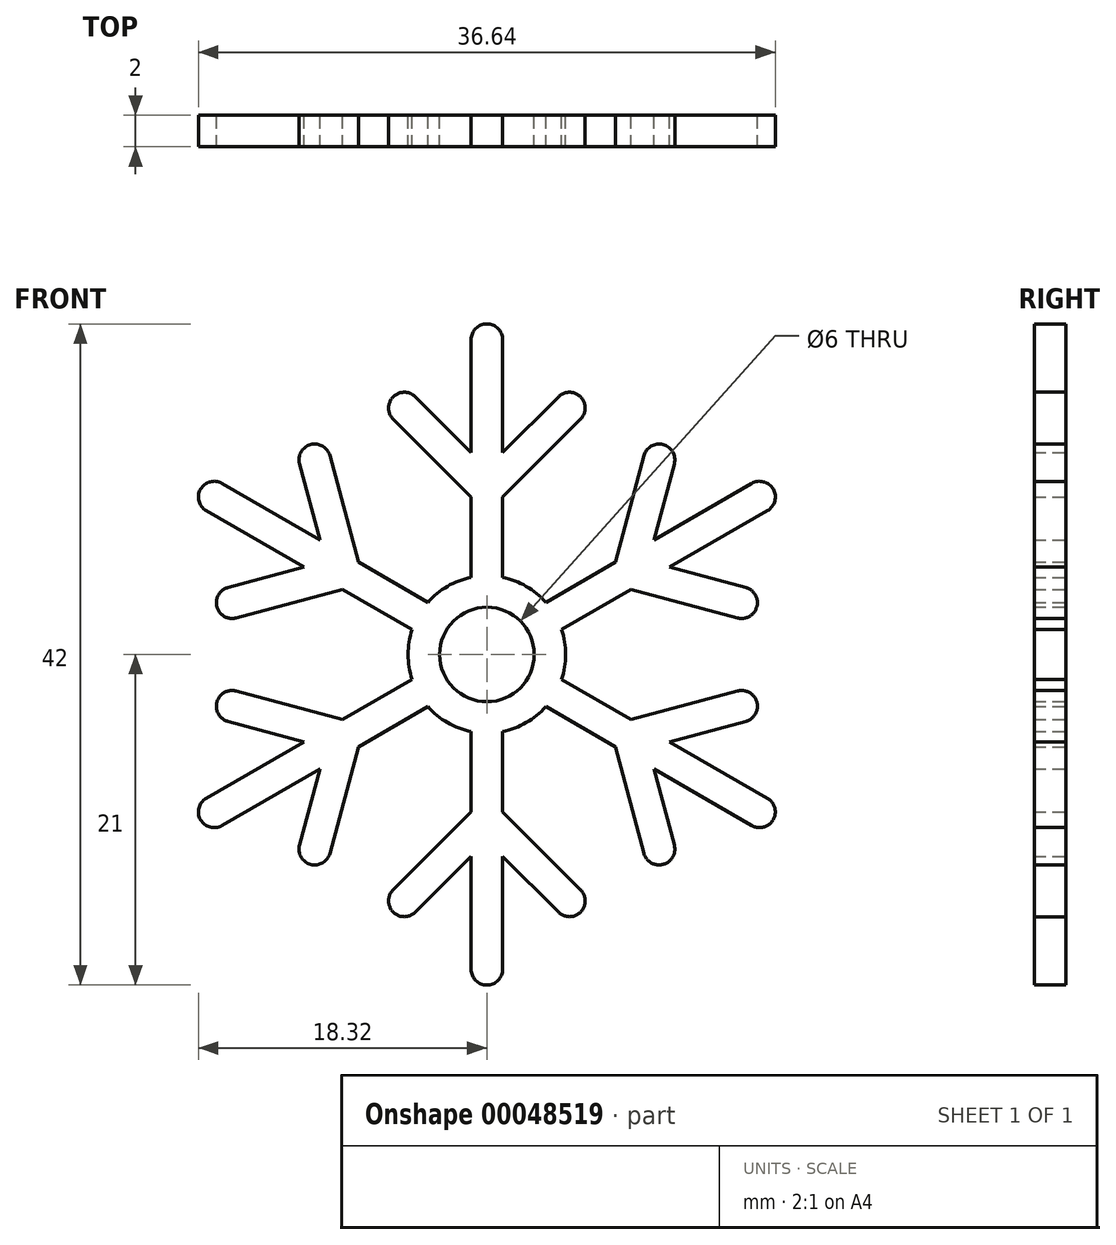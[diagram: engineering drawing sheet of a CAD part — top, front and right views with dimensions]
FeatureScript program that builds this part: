
annotation { "Feature Type Name" : "Feature", "Feature Type Description" : "" }
export const myFeature = defineFeature(function(context is Context, id is Id, definition is map)
    precondition{}
    {
        {
            var Q0;
            Q0=qCreatedBy(makeId("Front.planeOp"),FACE);
            var sketch = newSketch(context, id + "F0", { "sketchPlane" : qUnion([Q0])});
            skLineSegment(sketch, "E0", {"start": v(0, 14.92) * mm, "end": v(0, -7.22) * mm, "construction": true});
            skArc(sketch, "E1", {"start": v(-1, 4.9) * mm, "mid": v(-2.5, 4.33) * mm, "end": v(-3.74, 3.32) * mm});
            skCircle(sketch, "E2", {"center": v(0, 0) * mm, "radius": 3 * mm});
            skLineSegment(sketch, "E3", {"start": v(-1, 4.9) * mm, "end": v(-1, 10) * mm});
            skLineSegment(sketch, "E4", {"start": v(-1, 10) * mm, "end": v(-5.95, 14.95) * mm});
            skArc(sketch, "E5", {"start": v(-5.95, 14.95) * mm, "mid": v(-5.95, 16.36) * mm, "end": v(-4.54, 16.36) * mm});
            skLineSegment(sketch, "E6", {"start": v(-4.54, 16.36) * mm, "end": v(-1, 12.83) * mm});
            skLineSegment(sketch, "E7", {"start": v(-1, 12.83) * mm, "end": v(-1, 20) * mm});
            skArc(sketch, "E8", {"start": v(-1, 20) * mm, "mid": v(0.06, 21) * mm, "end": v(1, 19.87) * mm});
            skLineSegment(sketch, "E9.MirrorCS", {"start": v(1, 12.83) * mm, "end": v(1, 20) * mm});
            skLineSegment(sketch, "E10.MirrorCS", {"start": v(4.54, 16.36) * mm, "end": v(1, 12.83) * mm});
            skArc(sketch, "E11.MirrorCS", {"start": v(5.95, 14.95) * mm, "mid": v(5.95, 16.36) * mm, "end": v(4.54, 16.36) * mm});
            skLineSegment(sketch, "E12.MirrorCS", {"start": v(1, 10) * mm, "end": v(5.95, 14.95) * mm});
            skLineSegment(sketch, "E13.MirrorCS", {"start": v(1, 4.9) * mm, "end": v(1, 10) * mm});
            skPoint(sketch, "E14.orphan", {"position": v(1, 2.83) * mm});
            skPoint(sketch, "E15.orphan", {"position": v(-1, 2.83) * mm});
            skLineSegment(sketch, "E16.1.0", {"start": v(-3.74, 3.32) * mm, "end": v(-8.16, 5.87) * mm});
            skLineSegment(sketch, "E16.1.1", {"start": v(-8.16, 5.87) * mm, "end": v(-9.97, 12.63) * mm});
            skArc(sketch, "E16.1.2", {"start": v(-9.97, 12.63) * mm, "mid": v(-11.2, 13.33) * mm, "end": v(-11.9, 12.1) * mm});
            skLineSegment(sketch, "E16.1.3", {"start": v(-11.9, 12.1) * mm, "end": v(-10.6, 7.28) * mm});
            skLineSegment(sketch, "E16.1.4", {"start": v(-10.6, 7.28) * mm, "end": v(-16.82, 10.87) * mm});
            skArc(sketch, "E16.1.5", {"start": v(-17.82, 9.13) * mm, "mid": v(-18.15, 10.56) * mm, "end": v(-16.71, 10.8) * mm});
            skLineSegment(sketch, "E16.1.6", {"start": v(-11.6, 5.55) * mm, "end": v(-17.82, 9.13) * mm});
            skLineSegment(sketch, "E16.1.7", {"start": v(-16.44, 4.25) * mm, "end": v(-11.6, 5.55) * mm});
            skArc(sketch, "E16.1.8", {"start": v(-15.92, 2.32) * mm, "mid": v(-17.15, 3.03) * mm, "end": v(-16.44, 4.25) * mm});
            skLineSegment(sketch, "E16.1.9", {"start": v(-9.16, 4.13) * mm, "end": v(-15.92, 2.32) * mm});
            skLineSegment(sketch, "E16.1.10", {"start": v(-4.74, 1.58) * mm, "end": v(-9.16, 4.13) * mm});
            skLineSegment(sketch, "E16.2.0", {"start": v(-4.74, -1.58) * mm, "end": v(-9.16, -4.13) * mm});
            skLineSegment(sketch, "E16.2.1", {"start": v(-9.16, -4.13) * mm, "end": v(-15.92, -2.32) * mm});
            skArc(sketch, "E16.2.2", {"start": v(-15.92, -2.32) * mm, "mid": v(-17.15, -3.03) * mm, "end": v(-16.44, -4.25) * mm});
            skLineSegment(sketch, "E16.2.3", {"start": v(-16.44, -4.25) * mm, "end": v(-11.6, -5.55) * mm});
            skLineSegment(sketch, "E16.2.4", {"start": v(-11.6, -5.55) * mm, "end": v(-17.82, -9.13) * mm});
            skArc(sketch, "E16.2.5", {"start": v(-16.82, -10.87) * mm, "mid": v(-18.22, -10.44) * mm, "end": v(-17.7, -9.08) * mm});
            skLineSegment(sketch, "E16.2.6", {"start": v(-10.6, -7.28) * mm, "end": v(-16.82, -10.87) * mm});
            skLineSegment(sketch, "E16.2.7", {"start": v(-11.9, -12.1) * mm, "end": v(-10.6, -7.28) * mm});
            skArc(sketch, "E16.2.8", {"start": v(-9.97, -12.63) * mm, "mid": v(-11.2, -13.33) * mm, "end": v(-11.9, -12.1) * mm});
            skLineSegment(sketch, "E16.2.9", {"start": v(-8.16, -5.87) * mm, "end": v(-9.97, -12.63) * mm});
            skLineSegment(sketch, "E16.2.10", {"start": v(-3.74, -3.32) * mm, "end": v(-8.16, -5.87) * mm});
            skLineSegment(sketch, "E17.1.3.0", {"start": v(-1, -4.9) * mm, "end": v(-1, -10) * mm});
            skLineSegment(sketch, "E17.3.3.0", {"start": v(-1, -10) * mm, "end": v(-5.95, -14.95) * mm});
            skArc(sketch, "E17.6.3.0", {"start": v(-5.95, -14.95) * mm, "mid": v(-5.95, -16.36) * mm, "end": v(-4.54, -16.36) * mm});
            skLineSegment(sketch, "E17.10.3.0", {"start": v(-4.54, -16.36) * mm, "end": v(-1, -12.83) * mm});
            skLineSegment(sketch, "E17.13.3.0", {"start": v(-1, -12.83) * mm, "end": v(-1, -20) * mm});
            skArc(sketch, "E17.16.3.0", {"start": v(1, -20) * mm, "mid": v(-0.06, -21) * mm, "end": v(-1, -19.87) * mm});
            skLineSegment(sketch, "E17.20.3.0", {"start": v(1, -12.83) * mm, "end": v(1, -20) * mm});
            skLineSegment(sketch, "E17.23.3.0", {"start": v(4.54, -16.36) * mm, "end": v(1, -12.83) * mm});
            skArc(sketch, "E17.26.3.0", {"start": v(5.95, -14.95) * mm, "mid": v(5.95, -16.36) * mm, "end": v(4.54, -16.36) * mm});
            skLineSegment(sketch, "E17.30.3.0", {"start": v(1, -10) * mm, "end": v(5.95, -14.95) * mm});
            skLineSegment(sketch, "E17.33.3.0", {"start": v(1, -4.9) * mm, "end": v(1, -10) * mm});
            skLineSegment(sketch, "E17.1.4.0", {"start": v(3.74, -3.32) * mm, "end": v(8.16, -5.87) * mm});
            skLineSegment(sketch, "E17.3.4.0", {"start": v(8.16, -5.87) * mm, "end": v(9.97, -12.63) * mm});
            skArc(sketch, "E17.6.4.0", {"start": v(9.97, -12.63) * mm, "mid": v(11.2, -13.33) * mm, "end": v(11.9, -12.1) * mm});
            skLineSegment(sketch, "E17.10.4.0", {"start": v(11.9, -12.1) * mm, "end": v(10.6, -7.28) * mm});
            skLineSegment(sketch, "E17.13.4.0", {"start": v(10.6, -7.28) * mm, "end": v(16.82, -10.87) * mm});
            skArc(sketch, "E17.16.4.0", {"start": v(17.82, -9.13) * mm, "mid": v(18.15, -10.56) * mm, "end": v(16.71, -10.8) * mm});
            skLineSegment(sketch, "E17.20.4.0", {"start": v(11.6, -5.55) * mm, "end": v(17.82, -9.13) * mm});
            skLineSegment(sketch, "E17.23.4.0", {"start": v(16.44, -4.25) * mm, "end": v(11.6, -5.55) * mm});
            skArc(sketch, "E17.26.4.0", {"start": v(15.92, -2.32) * mm, "mid": v(17.15, -3.03) * mm, "end": v(16.44, -4.25) * mm});
            skLineSegment(sketch, "E17.30.4.0", {"start": v(9.16, -4.13) * mm, "end": v(15.92, -2.32) * mm});
            skLineSegment(sketch, "E17.33.4.0", {"start": v(4.74, -1.58) * mm, "end": v(9.16, -4.13) * mm});
            skLineSegment(sketch, "E17.1.5.0", {"start": v(4.74, 1.58) * mm, "end": v(9.16, 4.13) * mm});
            skLineSegment(sketch, "E17.3.5.0", {"start": v(9.16, 4.13) * mm, "end": v(15.92, 2.32) * mm});
            skArc(sketch, "E17.6.5.0", {"start": v(15.92, 2.32) * mm, "mid": v(17.15, 3.03) * mm, "end": v(16.44, 4.25) * mm});
            skLineSegment(sketch, "E17.10.5.0", {"start": v(16.44, 4.25) * mm, "end": v(11.6, 5.55) * mm});
            skLineSegment(sketch, "E17.13.5.0", {"start": v(11.6, 5.55) * mm, "end": v(17.82, 9.13) * mm});
            skArc(sketch, "E17.16.5.0", {"start": v(16.82, 10.87) * mm, "mid": v(18.22, 10.44) * mm, "end": v(17.7, 9.08) * mm});
            skLineSegment(sketch, "E17.20.5.0", {"start": v(10.6, 7.28) * mm, "end": v(16.82, 10.87) * mm});
            skLineSegment(sketch, "E17.23.5.0", {"start": v(11.9, 12.1) * mm, "end": v(10.6, 7.28) * mm});
            skArc(sketch, "E17.26.5.0", {"start": v(9.97, 12.63) * mm, "mid": v(11.2, 13.33) * mm, "end": v(11.9, 12.1) * mm});
            skLineSegment(sketch, "E17.30.5.0", {"start": v(8.16, 5.87) * mm, "end": v(9.97, 12.63) * mm});
            skLineSegment(sketch, "E17.33.5.0", {"start": v(3.74, 3.32) * mm, "end": v(8.16, 5.87) * mm});
            skArc(sketch, "E18.trimOffspring", {"start": v(3.74, 3.32) * mm, "mid": v(2.5, 4.33) * mm, "end": v(1, 4.9) * mm});
            skArc(sketch, "E19.trimOffspring", {"start": v(-4.74, 1.58) * mm, "mid": v(-5, 0) * mm, "end": v(-4.74, -1.58) * mm});
            skArc(sketch, "E20.trimOffspring", {"start": v(4.74, -1.58) * mm, "mid": v(5, 0) * mm, "end": v(4.74, 1.58) * mm});
            skArc(sketch, "E21.trimOffspring", {"start": v(1, -4.9) * mm, "mid": v(2.5, -4.33) * mm, "end": v(3.74, -3.32) * mm});
            skArc(sketch, "E22.trimOffspring", {"start": v(-3.74, -3.32) * mm, "mid": v(-2.5, -4.33) * mm, "end": v(-1, -4.9) * mm});
            skSolve(sketch);
        }
        {
            var Q0;
            Q0=makeQuery(id+"F0.imprint","IMPRINT",FACE,{"disambiguationData":[TD([[makeQuery(id+"F0.imprint","IMPRINT",EDGE,{"derivedFrom":sQuery(id+"F0.wireOp",EDGE,"E1")}),1.0]])]});
            extrude(context, id + "F1", {"entities" : qUnion([Q0]), "depth" : 2 * mm});
        }
    });
